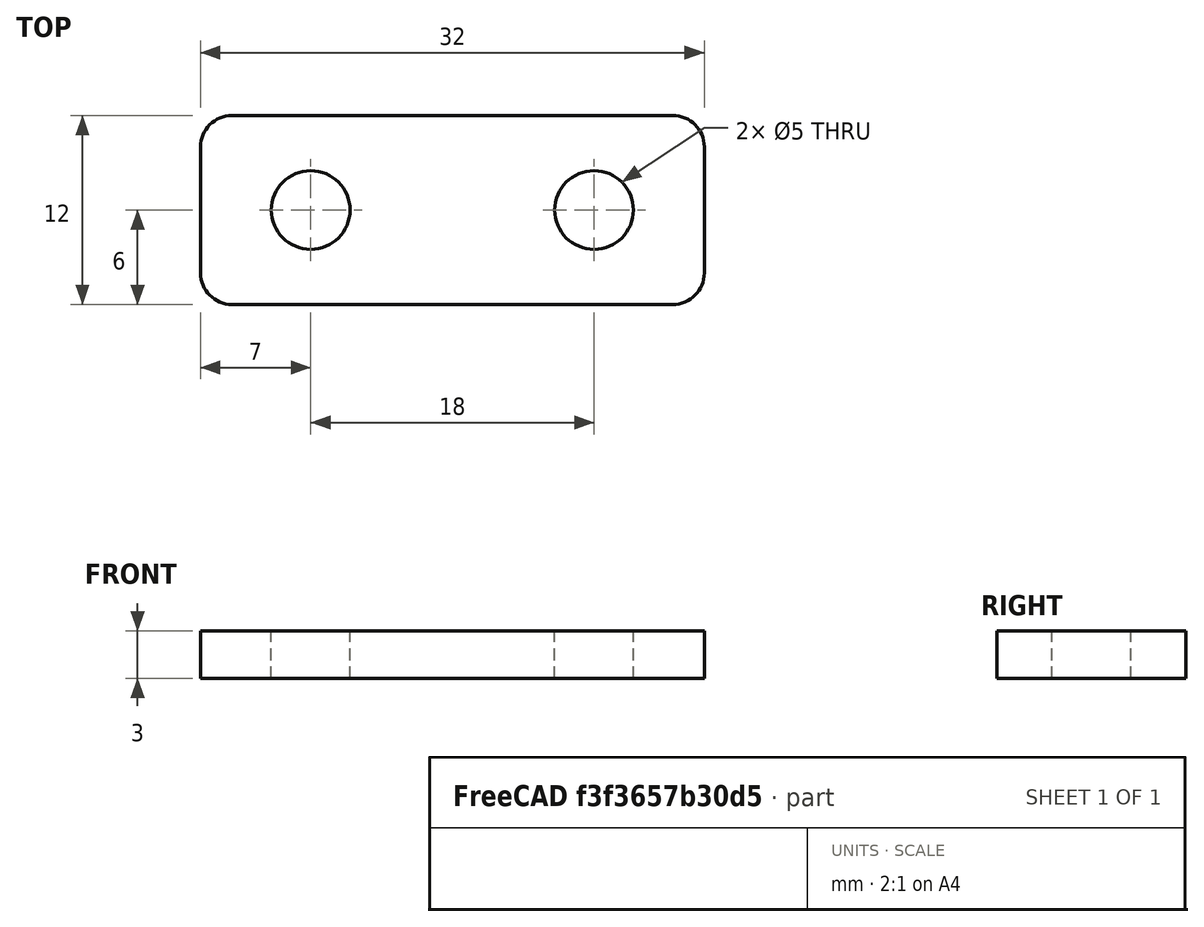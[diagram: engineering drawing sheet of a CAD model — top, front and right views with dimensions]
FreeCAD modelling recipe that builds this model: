
FCSTD DOCUMENT  (FreeCAD 0.17R13541 (Git))
Label: SujetaCable18mm
License: All rights reserved
LicenseURL: http://en.wikipedia.org/wiki/All_rights_reserved
objects: Part::Cylinder×2, Part::Box×1, Part::MultiFuse×1, Part::Cut×1, Part::Fillet×1, Part::Feature×1
note: 7 computed .brp shape members not serialized (recipe doc carries the construction recipe); baked Part::Feature solids carry a one-line shape summary decoded from their .brp

FEATURE [Part::Box] Box  label="Cubo"
  AttacherType = Attacher::AttachEngine3D
  Height = 3
  Length = 32
  Width = 12
FEATURE [Part::Cylinder] Cylinder  label="Cilindro"
  Angle = 360
  AttacherType = Attacher::AttachEngine3D
  Height = 10
  Placement = pos=(7,6,0) rot=(0,0,1;0rad)
  Radius = 2.5
FEATURE [Part::Cylinder] Cylinder001  label="Cilindro001"
  Angle = 360
  AttacherType = Attacher::AttachEngine3D
  Height = 10
  Placement = pos=(25,6,0) rot=(0,0,1;0rad)
  Radius = 2.5
FEATURE [Part::MultiFuse] Fusion
  Refine = true
  Shapes = -> [Cylinder001,Cylinder]
FEATURE [Part::Cut] Cut
  Base = -> Box
  Refine = true
  Tool = -> Fusion
FEATURE [Part::Fillet] Fillet  label="SujetaCable18mm-Terminado"
  Base = -> Cut
  Edges = 4 edges r=2: [Edge1,Edge3,Edge6,Edge13]
FEATURE [Part::Feature] Fillet001  label="SujetaCable18mm-CopiaSimple"
  shape: bbox 32 x 12 x 3 mm, 12 faces (baked)
